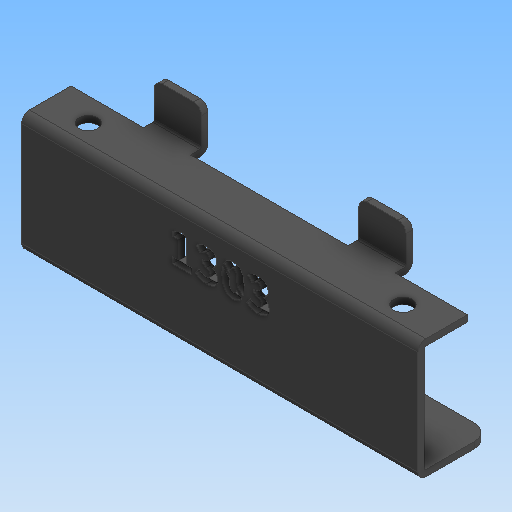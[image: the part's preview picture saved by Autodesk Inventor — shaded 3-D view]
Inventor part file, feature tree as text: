
AUTODESK INVENTOR PART (.ipt)
format: ipt  version: 2020 (Build 240168000, 168)  size: 538,624 bytes
history: native  units: mm
features: other x5, extrude x3, fillet x1, sketch x1, projected_geometry x1
ambient origin geometry x8: Origin, YZ Plane, XZ Plane, XY Plane, X Axis, Y Axis, Z Axis, Center Point
bodies: Body1 (feature_tree)
feature tree (11):
  other  "實體1"
  extrude  "擠出1"  Depth=126.0mm
  extrude  "擠出3"  Depth=21.3mm
  extrude  "擠出4"  Depth=33.0mm
  other  "折彎零件3"
  other  "折彎零件1"
  other  "折彎零件2"
  fillet  "圓角1"  Radius=14.0mm
  sketch  "草圖4"
  projected_geometry  "投影迴路1"
  other  "定義1"
